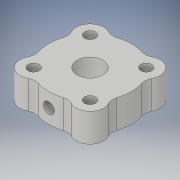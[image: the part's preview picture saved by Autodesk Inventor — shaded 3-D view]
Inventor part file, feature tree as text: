
AUTODESK INVENTOR PART (.ipt)
format: ipt  version: 2019 (Build 230136000, 136)  size: 147,456 bytes
history: native  units: mm
features: fillet x1
ambient origin geometry x8: Origin, YZ Plane, XZ Plane, XY Plane, X Axis, Y Axis, Z Axis, Center Point
bodies: Solid1 (feature_tree)
feature tree (1):
  fillet  "Fillet1"  [1 undecoded]
note: 1 required parameter value undecoded (feature->parameter linkage not recoverable at this tier; creation-order binding heuristic only, values carry confidence <= 0.55)
